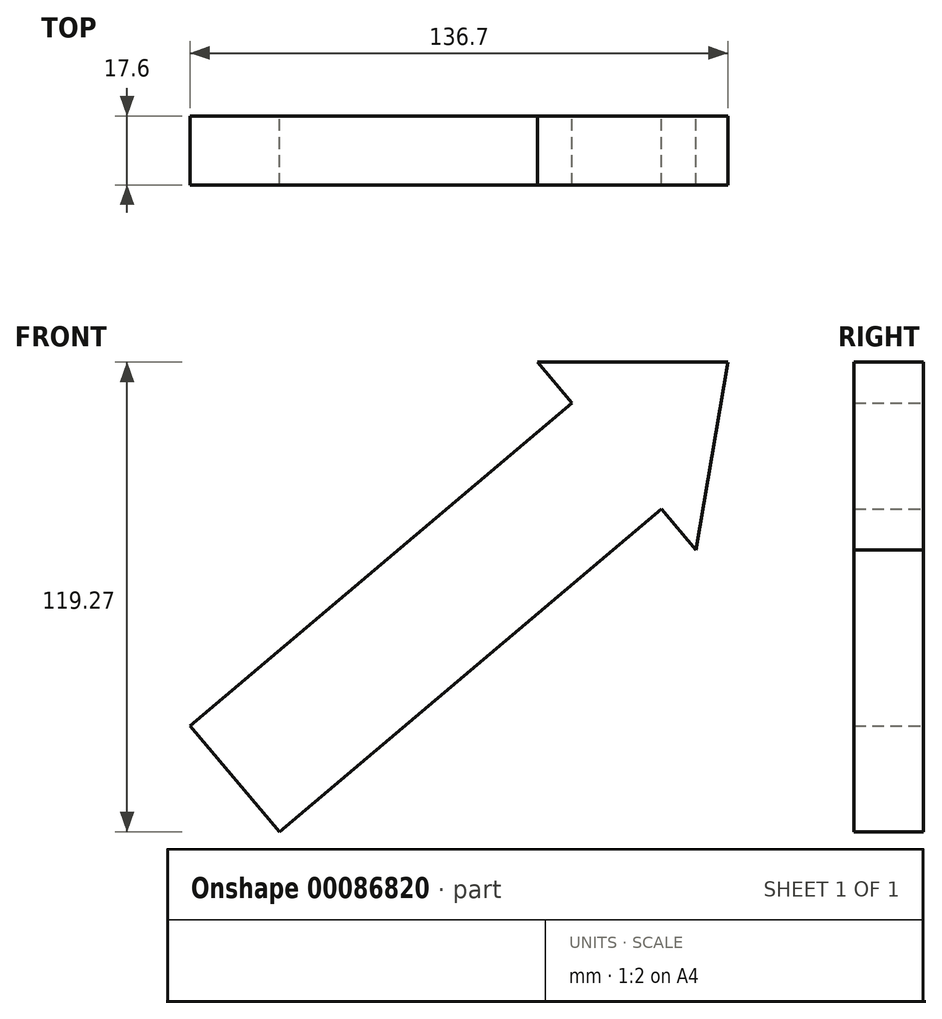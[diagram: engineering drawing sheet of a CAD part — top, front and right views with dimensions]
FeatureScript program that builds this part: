
annotation { "Feature Type Name" : "Feature", "Feature Type Description" : "" }
export const myFeature = defineFeature(function(context is Context, id is Id, definition is map)
    precondition{}
    {
        {
            var Q0;
            Q0=qCreatedBy(makeId("Front.planeOp"),FACE);
            var sketch = newSketch(context, id + "F0", { "sketchPlane" : qUnion([Q0])});
            skLineSegment(sketch, "E0", {"start": v(0, 0) * mm, "end": v(97.04, 81.92) * mm});
            skLineSegment(sketch, "E1", {"start": v(97.04, 81.92) * mm, "end": v(88.25, 92.34) * mm});
            skLineSegment(sketch, "E2", {"start": v(88.25, 92.34) * mm, "end": v(136.7, 92.34) * mm});
            skLineSegment(sketch, "E3", {"start": v(0, -23.06) * mm, "end": v(130.86, 87.4) * mm, "construction": true});
            skLineSegment(sketch, "E4.MirrorCS", {"start": v(22.73, -26.93) * mm, "end": v(119.78, 55) * mm});
            skLineSegment(sketch, "E5.MirrorCS", {"start": v(119.78, 55) * mm, "end": v(128.57, 44.58) * mm});
            skLineSegment(sketch, "E6.MirrorCS", {"start": v(128.57, 44.58) * mm, "end": v(136.7, 92.34) * mm});
            skLineSegment(sketch, "E7", {"start": v(0, 0) * mm, "end": v(22.73, -26.93) * mm});
            skSolve(sketch);
        }
        {
            var Q0;
            Q0=makeQuery(id+"F0.imprint","IMPRINT",FACE,{"disambiguationData":[TD([[makeQuery(id+"F0.imprint","IMPRINT",EDGE,{"derivedFrom":sQuery(id+"F0.wireOp",EDGE,"E0")}),-1.0]])]});
            extrude(context, id + "F1", {"entities" : qUnion([Q0]), "depth" : 17.6 * mm});
        }
    });
